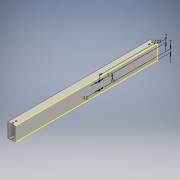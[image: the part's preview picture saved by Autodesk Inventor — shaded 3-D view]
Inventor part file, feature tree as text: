
AUTODESK INVENTOR PART (.ipt)
format: ipt  version: 2019 (Build 230136000, 136)  size: 137,216 bytes
history: native  units: mm
features: sketch x3, other x1, extrude x1, hole x1
ambient origin geometry x8: Origin, YZ Plane, XZ Plane, XY Plane, X Axis, Y Axis, Z Axis, Center Point
bodies: Body1 (feature_tree)
feature tree (6):
  other  "ソリッド1"
  extrude  "押し出し1"  Depth=15.0mm
  hole  "穴1"  [1 undecoded]
  sketch  "スケッチ3"
  sketch  "スケッチ1"
  sketch  "スケッチ2"
note: 1 required parameter value undecoded (feature->parameter linkage not recoverable at this tier; creation-order binding heuristic only, values carry confidence <= 0.55)
